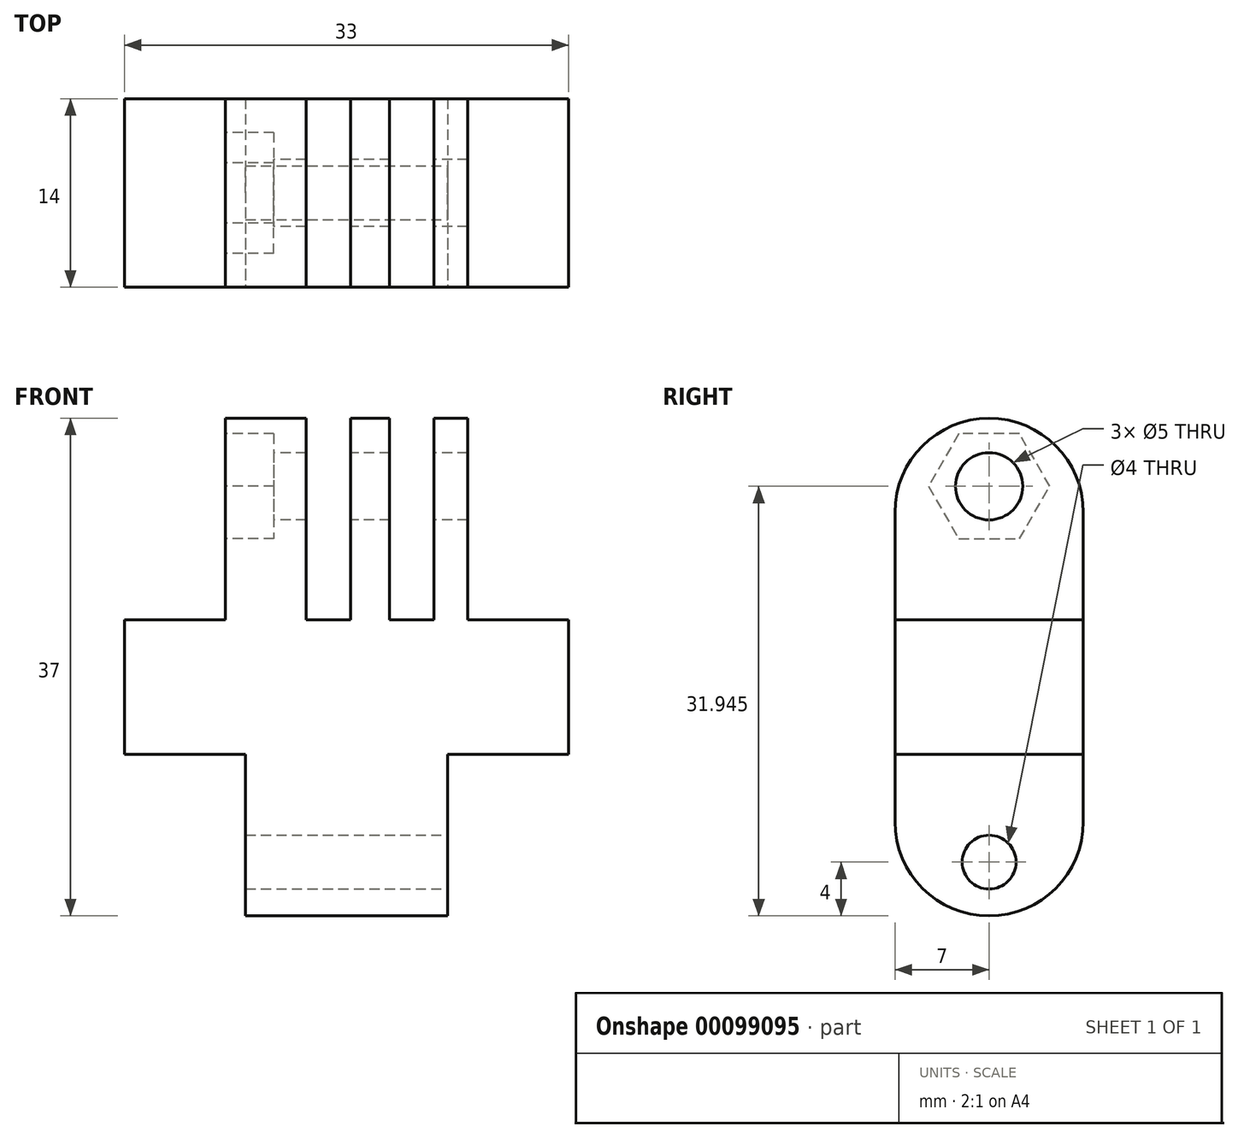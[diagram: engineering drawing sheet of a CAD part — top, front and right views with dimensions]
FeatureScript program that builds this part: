
annotation { "Feature Type Name" : "Feature", "Feature Type Description" : "" }
export const myFeature = defineFeature(function(context is Context, id is Id, definition is map)
    precondition{}
    {
        {
            var Q0;
            Q0=qCreatedBy(makeId("Top.planeOp"),FACE);
            var sketch = newSketch(context, id + "F0", { "sketchPlane" : qUnion([Q0])});
            skLineSegment(sketch, "E0.bottom", {"start": v(0, 0) * mm, "end": v(33, 0) * mm});
            skLineSegment(sketch, "E0.top", {"start": v(0, -14) * mm, "end": v(33, -14) * mm});
            skLineSegment(sketch, "E0.left", {"start": v(0, 0) * mm, "end": v(0, -14) * mm});
            skLineSegment(sketch, "E0.right", {"start": v(33, 0) * mm, "end": v(33, -14) * mm});
            skSolve(sketch);
        }
        {
            var Q0;
            Q0=makeQuery(id+"F0.imprint","IMPRINT",FACE,{"disambiguationData":[TD([[makeQuery(id+"F0.imprint","IMPRINT",EDGE,{"derivedFrom":sQuery(id+"F0.wireOp",EDGE,"E0.bottom")}),-1.0]])]});
            extrude(context, id + "F1", {"entities" : qUnion([Q0]), "depth" : 10 * mm});
        }
        {
            var Q0;
            Q0=makeQuery(id+"F1.opExtrude","CAP_FACE",FACE,{"disambiguationData":[OSD([sQuery(id+"F0.wireOp",EDGE,"E0.bottom"),sQuery(id+"F0.wireOp",EDGE,"E0.top"),sQuery(id+"F0.wireOp",EDGE,"E0.left"),sQuery(id+"F0.wireOp",EDGE,"E0.right")])],"isStart":true});
            var sketch = newSketch(context, id + "F2", { "sketchPlane" : qUnion([Q0])});
            skLineSegment(sketch, "E1.bottom", {"start": v(9, 0) * mm, "end": v(24, 0) * mm});
            skLineSegment(sketch, "E1.top", {"start": v(9, 14) * mm, "end": v(24, 14) * mm});
            skLineSegment(sketch, "E1.left", {"start": v(9, 0) * mm, "end": v(9, 14) * mm});
            skLineSegment(sketch, "E1.right", {"start": v(24, 0) * mm, "end": v(24, 14) * mm});
            skSolve(sketch);
        }
        {
            var Q0;
            Q0=makeQuery(id+"F2.imprint","IMPRINT",FACE,{"disambiguationData":[TD([[makeQuery(id+"F2.imprint","IMPRINT",EDGE,{"derivedFrom":sQuery(id+"F2.wireOp",EDGE,"E1.bottom")}),1.0]])]});
            extrude(context, id + "F3", {"entities" : qUnion([Q0]), "operationType" : NewBodyOperationType.ADD, "depth" : 12 * mm});
        }
        {
            var Q0;
            Q0=makeQuery(id+"F3.opExtrude","CAP_EDGE",EDGE,{"disambiguationData":[OSD([sQuery(id+"F2.wireOp",EDGE,"E1.bottom")])],"isStart":false});
            fillet(context, id + "F4", {"entities" : qUnion([Q0]), "radius" : 7 * mm, "tangentPropagation" : true, "allowEdgeOverflow" : false});
        }
        {
            var Q0;
            Q0=makeQuery(id+"F3.opExtrude","CAP_EDGE",EDGE,{"disambiguationData":[OSD([sQuery(id+"F2.wireOp",EDGE,"E1.top")])],"isStart":false});
            fillet(context, id + "F5", {"entities" : qUnion([Q0]), "radius" : 7 * mm, "tangentPropagation" : true, "allowEdgeOverflow" : false});
        }
        {
            var Q0;
            Q0=makeQuery(id+"F3.opExtrude","SWEPT_FACE",FACE,{"disambiguationData":[OSD([sQuery(id+"F2.wireOp",EDGE,"E1.right")])]});
            var sketch = newSketch(context, id + "F6", { "sketchPlane" : qUnion([Q0])});
            skCircle(sketch, "E2", {"center": v(-7, -8) * mm, "radius": 2 * mm});
            skLineSegment(sketch, "E3", {"start": v(-7, 0) * mm, "end": v(-7, -12) * mm});
            skSolve(sketch);
        }
        {
            var Q0;
            {var subQ0=sQuery(id+"F6.wireOp",EDGE,"E3");var subQ1=sQuery(id+"F6.wireOp",EDGE,"E2");var subQ2=makeQuery(id+"F6.imprint","INTERSECT",VERTEX,{"disambiguationData":[OD(0.0)],"derivedFrom":[subQ1,subQ0]});Q0=makeQuery(id+"F6.imprint","IMPRINT",FACE,{"disambiguationData":[TD([[makeQuery(id+"F6.imprint","IMPRINT",EDGE,{"disambiguationData":[TD([[subQ2,-1.0]])],"derivedFrom":subQ1}),1.0]])]});}
            var Q1;
            {var subQ0=sQuery(id+"F6.wireOp",EDGE,"E3");var subQ1=sQuery(id+"F6.wireOp",EDGE,"E2");var subQ2=makeQuery(id+"F6.imprint","INTERSECT",VERTEX,{"disambiguationData":[OD(0.0)],"derivedFrom":[subQ1,subQ0]});Q1=makeQuery(id+"F6.imprint","IMPRINT",FACE,{"disambiguationData":[TD([[makeQuery(id+"F6.imprint","IMPRINT",EDGE,{"disambiguationData":[TD([[subQ2,1.0]])],"derivedFrom":subQ1}),1.0]])]});}
            extrude(context, id + "F7", {"entities" : qUnion([Q0, Q1]), "operationType" : NewBodyOperationType.REMOVE, "endBound" : BoundingType.THROUGH_ALL, "oppositeDirection" : true, "depth" : 25 * mm});
        }
        {
            var Q0;
            Q0=makeQuery(id+"F1.opExtrude","CAP_FACE",FACE,{"disambiguationData":[OSD([sQuery(id+"F0.wireOp",EDGE,"E0.bottom"),sQuery(id+"F0.wireOp",EDGE,"E0.top"),sQuery(id+"F0.wireOp",EDGE,"E0.left"),sQuery(id+"F0.wireOp",EDGE,"E0.right")])],"isStart":false});
            var sketch = newSketch(context, id + "F8", { "sketchPlane" : qUnion([Q0])});
            skLineSegment(sketch, "E4.bottom", {"start": v(7.5, 0) * mm, "end": v(25.5, 0) * mm});
            skLineSegment(sketch, "E4.top", {"start": v(7.5, -14) * mm, "end": v(25.5, -14) * mm});
            skLineSegment(sketch, "E4.left", {"start": v(7.5, 0) * mm, "end": v(7.5, -14) * mm});
            skLineSegment(sketch, "E4.right", {"start": v(25.5, 0) * mm, "end": v(25.5, -14) * mm});
            skSolve(sketch);
        }
        {
            var Q0;
            Q0=makeQuery(id+"F8.imprint","IMPRINT",FACE,{"disambiguationData":[TD([[makeQuery(id+"F8.imprint","IMPRINT",EDGE,{"derivedFrom":sQuery(id+"F8.wireOp",EDGE,"E4.bottom")}),-1.0]])]});
            extrude(context, id + "F9", {"entities" : qUnion([Q0]), "operationType" : NewBodyOperationType.ADD, "depth" : 15 * mm});
        }
        {
            var Q0;
            Q0=makeQuery(id+"F9.opExtrude","SWEPT_FACE",FACE,{"disambiguationData":[OSD([sQuery(id+"F8.wireOp",EDGE,"E4.left")])]});
            var sketch = newSketch(context, id + "F10", { "sketchPlane" : qUnion([Q0])});
            skLineSegment(sketch, "E5", {"start": v(7, 10) * mm, "end": v(7, 24.94) * mm});
            skCircle(sketch, "E6", {"center": v(7, 19.94) * mm, "radius": 2.5 * mm});
            skSolve(sketch);
        }
        {
            var Q0;
            {var subQ0=sQuery(id+"F10.wireOp",EDGE,"E6");var subQ1=sQuery(id+"F10.wireOp",EDGE,"E5");var subQ2=makeQuery(id+"F10.imprint","INTERSECT",VERTEX,{"disambiguationData":[OD(0.0)],"derivedFrom":[subQ1,subQ0]});Q0=makeQuery(id+"F10.imprint","IMPRINT",FACE,{"disambiguationData":[TD([[makeQuery(id+"F10.imprint","IMPRINT",EDGE,{"disambiguationData":[TD([[subQ2,-1.0]])],"derivedFrom":subQ1}),-1.0]])]});}
            var Q1;
            {var subQ0=sQuery(id+"F10.wireOp",EDGE,"E6");var subQ1=sQuery(id+"F10.wireOp",EDGE,"E5");var subQ2=makeQuery(id+"F10.imprint","INTERSECT",VERTEX,{"disambiguationData":[OD(0.0)],"derivedFrom":[subQ1,subQ0]});Q1=makeQuery(id+"F10.imprint","IMPRINT",FACE,{"disambiguationData":[TD([[makeQuery(id+"F10.imprint","IMPRINT",EDGE,{"disambiguationData":[TD([[subQ2,-1.0]])],"derivedFrom":subQ1}),1.0]])]});}
            extrude(context, id + "F11", {"entities" : qUnion([Q0, Q1]), "operationType" : NewBodyOperationType.REMOVE, "oppositeDirection" : true, "depth" : 25 * mm});
        }
        {
            var Q0;
            Q0=makeQuery(id+"F9.boolean.opBoolean","MERGE",FACE,{"derivedFrom":[makeQuery(id+"F3.boolean.opBoolean","MERGE",FACE,{"derivedFrom":[makeQuery(id+"F1.opExtrude","SWEPT_FACE",FACE,{"disambiguationData":[OSD([sQuery(id+"F0.wireOp",EDGE,"E0.top")])]}),makeQuery(id+"F3.opExtrude","SWEPT_FACE",FACE,{"disambiguationData":[OSD([sQuery(id+"F2.wireOp",EDGE,"E1.top")])]})]}),makeQuery(id+"F9.opExtrude","SWEPT_FACE",FACE,{"disambiguationData":[OSD([sQuery(id+"F8.wireOp",EDGE,"E4.top")])]})]});
            var sketch = newSketch(context, id + "F12", { "sketchPlane" : qUnion([Q0])});
            skLineSegment(sketch, "E7.bottom", {"start": v(13.5, 25.01) * mm, "end": v(16.8, 25.01) * mm});
            skLineSegment(sketch, "E7.top", {"start": v(13.5, 10) * mm, "end": v(16.8, 10) * mm});
            skLineSegment(sketch, "E7.left", {"start": v(13.5, 25.01) * mm, "end": v(13.5, 10) * mm});
            skLineSegment(sketch, "E7.right", {"start": v(16.8, 25.01) * mm, "end": v(16.8, 10) * mm});
            skLineSegment(sketch, "E8.bottom", {"start": v(19.7, 25.04) * mm, "end": v(23, 25.04) * mm});
            skLineSegment(sketch, "E8.top", {"start": v(19.7, 10) * mm, "end": v(23, 10) * mm});
            skLineSegment(sketch, "E8.left", {"start": v(19.7, 25.04) * mm, "end": v(19.7, 10) * mm});
            skLineSegment(sketch, "E8.right", {"start": v(23, 25.04) * mm, "end": v(23, 10) * mm});
            skSolve(sketch);
        }
        {
            var Q0;
            Q0=makeQuery(id+"F9.opExtrude","CAP_EDGE",EDGE,{"disambiguationData":[OSD([sQuery(id+"F8.wireOp",EDGE,"E4.top")])],"isStart":false});
            var Q1;
            Q1=makeQuery(id+"F9.opExtrude","CAP_EDGE",EDGE,{"disambiguationData":[OSD([sQuery(id+"F8.wireOp",EDGE,"E4.bottom")])],"isStart":false});
            fillet(context, id + "F13", {"entities" : qUnion([Q0, Q1]), "radius" : 7 * mm, "tangentPropagation" : true, "allowEdgeOverflow" : false});
        }
        {
            var Q0;
            {var subQ0=sQuery(id+"F12.wireOp",EDGE,"E8.top");Q0=makeQuery(id+"F12.imprint","IMPRINT",FACE,{"disambiguationData":[TD([[makeQuery(id+"F12.imprint","IMPRINT",EDGE,{"derivedFrom":subQ0}),1.0]])]});}
            var Q1;
            {var subQ0=sQuery(id+"F12.wireOp",EDGE,"E7.top");Q1=makeQuery(id+"F12.imprint","IMPRINT",FACE,{"disambiguationData":[TD([[makeQuery(id+"F12.imprint","IMPRINT",EDGE,{"derivedFrom":subQ0}),1.0]])]});}
            extrude(context, id + "F14", {"entities" : qUnion([Q0, Q1]), "operationType" : NewBodyOperationType.REMOVE, "oppositeDirection" : true, "depth" : 25 * mm});
        }
        {
            var Q0;
            Q0=makeQuery(id+"F9.opExtrude","SWEPT_FACE",FACE,{"disambiguationData":[OSD([sQuery(id+"F8.wireOp",EDGE,"E4.left")])]});
            var sketch = newSketch(context, id + "F15", { "sketchPlane" : qUnion([Q0])});
            skCircle(sketch, "E9.cCircle", {"center": v(7, 19.94) * mm, "radius": 3.9 * mm, "construction": true});
            skLineSegment(sketch, "E9.0", {"start": v(9.25, 16.04) * mm, "end": v(4.75, 16.04) * mm});
            skLineSegment(sketch, "E9.1", {"start": v(4.75, 16.04) * mm, "end": v(2.5, 19.94) * mm});
            skLineSegment(sketch, "E9.2", {"start": v(2.5, 19.94) * mm, "end": v(4.75, 23.84) * mm});
            skLineSegment(sketch, "E9.3", {"start": v(4.75, 23.84) * mm, "end": v(9.25, 23.84) * mm});
            skLineSegment(sketch, "E9.4", {"start": v(9.25, 23.84) * mm, "end": v(11.5, 19.94) * mm});
            skLineSegment(sketch, "E9.5", {"start": v(11.5, 19.94) * mm, "end": v(9.25, 16.04) * mm});
            skPoint(sketch, "E9.0.midPoint", {"position": v(7, 16.04) * mm});
            skSolve(sketch);
        }
        {
            var Q0;
            Q0=makeQuery(id+"F15.imprint","IMPRINT",FACE,{"disambiguationData":[TD([[makeQuery(id+"F15.imprint","IMPRINT",EDGE,{"derivedFrom":sQuery(id+"F15.wireOp",EDGE,"E9.0")}),-1.0]])]});
            extrude(context, id + "F16", {"entities" : qUnion([Q0]), "operationType" : NewBodyOperationType.REMOVE, "oppositeDirection" : true, "depth" : 3.6 * mm});
        }
    });
